# Revit family: QF_Marco_Mix_UC8
name_source: partatom
category: Specialty Equipment
units: mm (PartAtom-declared; Revit-internal decimal feet)

## family parameters
Always vertical = Yes
Cut with Voids When Loaded = No
Part Type = Normal
Room Calculation Point = No
Round Connector Dimension = Use Diameter
Shared = No
Work Plane-Based = No

## types (1)
- QF_Marco_Mix_UC8
    Apparent Power = 0 VA
    Cold Water Connection Height = 0 "
    Cold Water Flow = 0 GPM
    Cold Water Maximum Pressure = 0.00 psi
    Cold Water Minimum Pressure = 0.00 psi
    Cold Water RI Height = 0 "
    Cold Water Size = 1"
    Cold Water Temperature Recommended = 0 °F
    Conn Conduit = Yes
    Conn Plug = NEMA L6-20P
    Cycle = 60 Hz
    Depth = 13.862 "
    Description = Mix Countertop Multi-Temp Water Boilers/Push Button
    Elec Conn Connection Height = 0 "
    Elec Conn RI Height = 0 "
    FL Amps = 12 A
    Foodservice Equipment Identifier = Yes
    Height = 24.281 "
    Identify Quantity as Lot = Yes
    Indirect Waste Connection Height = 0 "
    Indirect Waste Flow = 0 GPM
    Indirect Waste Size = 1"
    Length = 8.268 "
    Manufacturer = Marco
    Max Overcurrent Protection = 0 A
    Min Ckt Ampacity = 0 A
    Model = MIX UC8
    Number of Poles = 1
    Phase = 1
    Volts = 230 V
    Waste Water Discharge Temperature = 0 °F
    Watts = 2800 W
    Weight in Pounds = 14

## geometry (parser evidence)
native form markers: Sweep x1
no freeform markers — native parametric forms only
